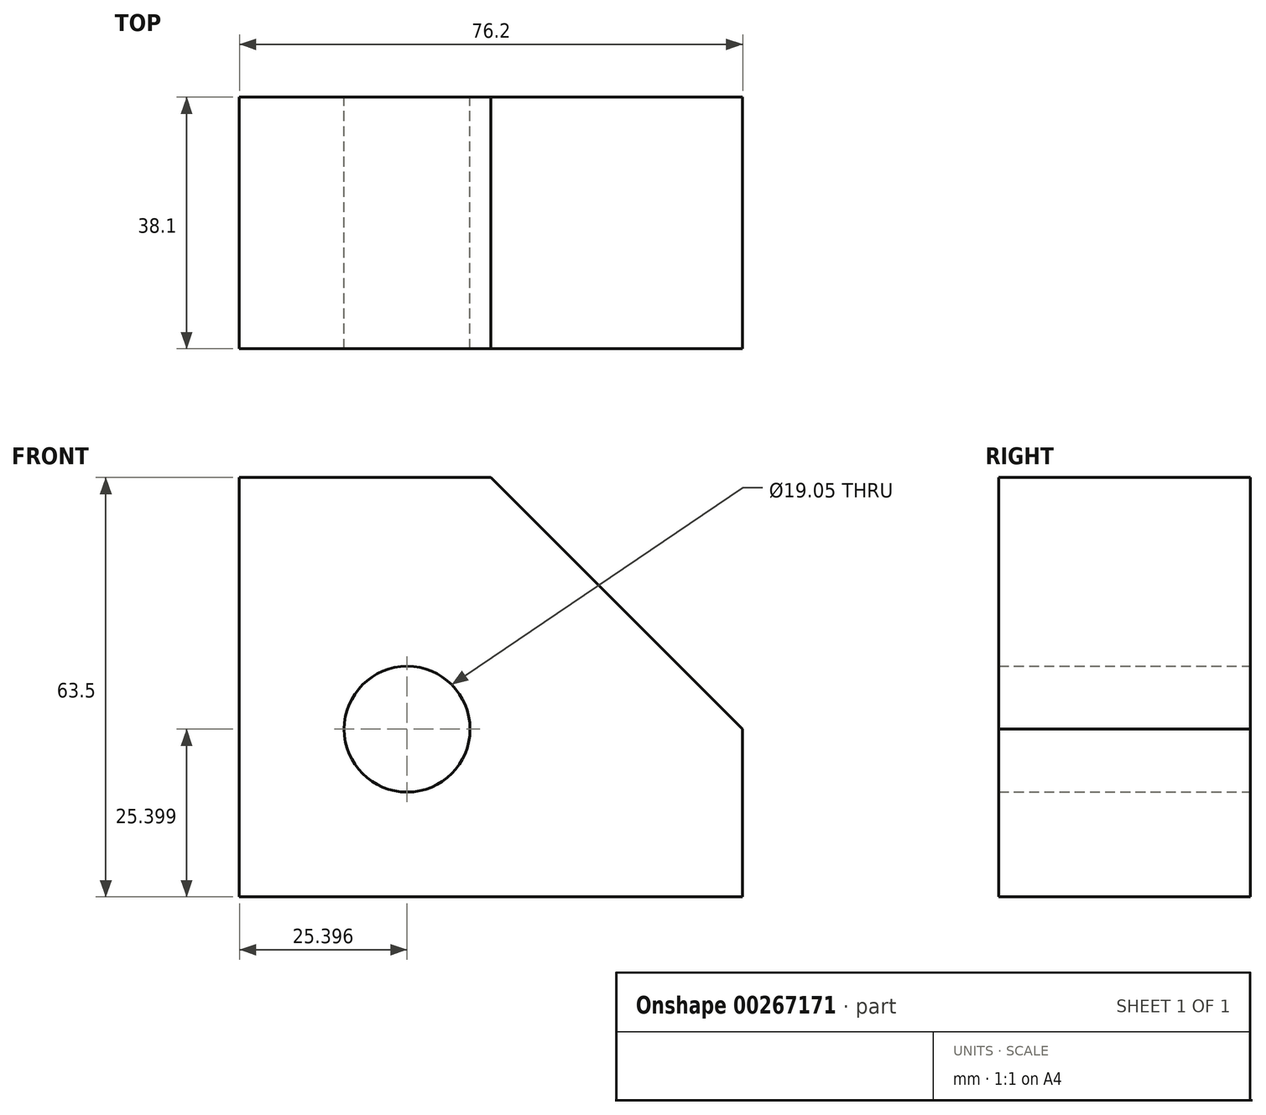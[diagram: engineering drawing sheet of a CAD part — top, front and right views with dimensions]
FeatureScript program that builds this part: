
annotation { "Feature Type Name" : "Feature", "Feature Type Description" : "" }
export const myFeature = defineFeature(function(context is Context, id is Id, definition is map)
    precondition{}
    {
        {
            var Q0;
            Q0=qCreatedBy(makeId("Front.planeOp"),FACE);
            var sketch = newSketch(context, id + "F0", { "sketchPlane" : qUnion([Q0])});
            skLineSegment(sketch, "E0", {"start": v(-34.6, -37.06) * mm, "end": v(41.6, -37.06) * mm});
            skLineSegment(sketch, "E1", {"start": v(41.6, -37.06) * mm, "end": v(41.6, -11.66) * mm});
            skLineSegment(sketch, "E2", {"start": v(41.6, -11.66) * mm, "end": v(3.5, 26.44) * mm});
            skLineSegment(sketch, "E3", {"start": v(3.5, 26.44) * mm, "end": v(-34.6, 26.44) * mm});
            skLineSegment(sketch, "E4", {"start": v(-34.6, 26.44) * mm, "end": v(-34.6, -37.06) * mm});
            skCircle(sketch, "E5", {"center": v(-9.2, -11.66) * mm, "radius": 9.53 * mm});
            skSolve(sketch);
        }
        {
            var Q0;
            Q0=makeQuery(id+"F0.imprint","IMPRINT",FACE,{"disambiguationData":[TD([[makeQuery(id+"F0.imprint","IMPRINT",EDGE,{"derivedFrom":sQuery(id+"F0.wireOp",EDGE,"E0")}),1.0]])]});
            extrude(context, id + "F1", {"entities" : qUnion([Q0]), "depth" : 38.1 * mm, "symmetric" : true});
        }
    });
